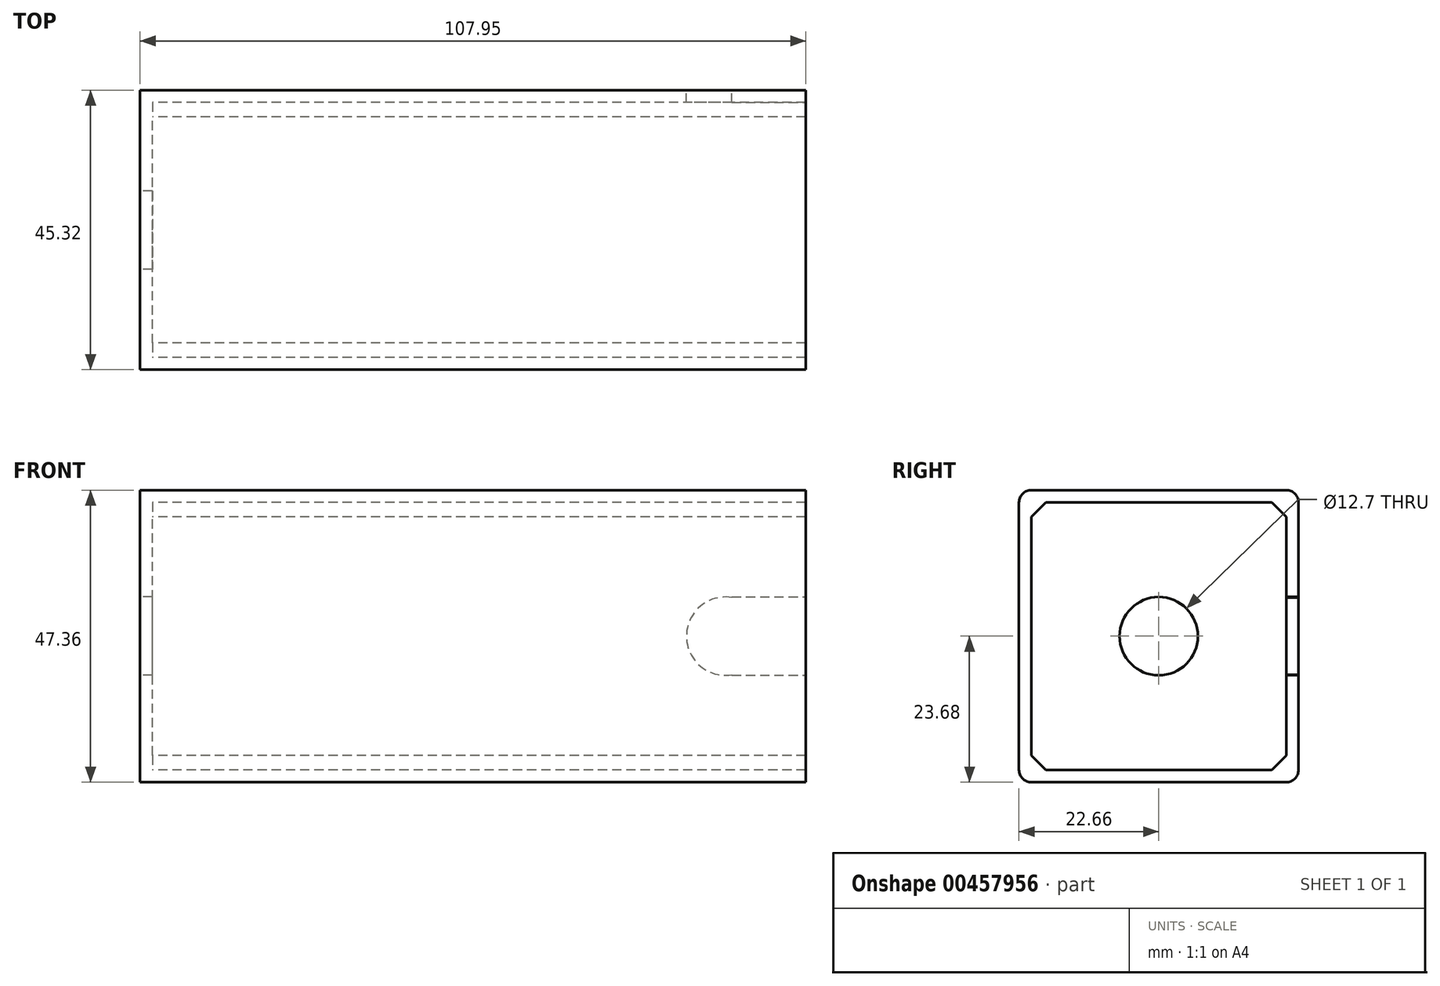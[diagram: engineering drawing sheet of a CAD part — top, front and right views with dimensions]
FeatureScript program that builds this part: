
annotation { "Feature Type Name" : "Feature", "Feature Type Description" : "" }
export const myFeature = defineFeature(function(context is Context, id is Id, definition is map)
    precondition{}
    {
        {
            assignVariable(context, id + "F0", {"name" : "WallWidth", "anyValue" : 2 * mm});
        }
        {
            var Q0;
            Q0=qCreatedBy(makeId("Right.planeOp"),FACE);
            var sketch = newSketch(context, id + "F1", { "sketchPlane" : qUnion([Q0])});
            skLineSegment(sketch, "E0.bottom", {"start": v(20.66, 21.68) * mm, "end": v(-20.66, 21.68) * mm});
            skLineSegment(sketch, "E0.top", {"start": v(20.66, -21.68) * mm, "end": v(-20.66, -21.68) * mm});
            skLineSegment(sketch, "E0.left", {"start": v(20.66, 21.68) * mm, "end": v(20.66, -21.68) * mm});
            skLineSegment(sketch, "E0.right", {"start": v(-20.66, 21.68) * mm, "end": v(-20.66, -21.68) * mm});
            skPoint(sketch, "E0.middle", {"position": v(0, 0) * mm});
            skLineSegment(sketch, "E1", {"start": v(-20.66, -19.34) * mm, "end": v(-18.32, -21.68) * mm});
            skLineSegment(sketch, "E2", {"start": v(18.32, -21.68) * mm, "end": v(20.65, -19.34) * mm});
            skLineSegment(sketch, "E3", {"start": v(-20.65, 19.34) * mm, "end": v(-18.32, 21.68) * mm});
            skLineSegment(sketch, "E4", {"start": v(18.32, 21.68) * mm, "end": v(20.65, 19.34) * mm});
            skLineSegment(sketch, "E5.bottom", {"start": v(-22.66, 23.68) * mm, "end": v(22.66, 23.68) * mm});
            skLineSegment(sketch, "E5.top", {"start": v(-22.66, -23.68) * mm, "end": v(22.66, -23.68) * mm});
            skLineSegment(sketch, "E5.left", {"start": v(-22.66, 23.68) * mm, "end": v(-22.66, -23.68) * mm});
            skLineSegment(sketch, "E5.right", {"start": v(22.66, 23.68) * mm, "end": v(22.66, -23.68) * mm});
            skSolve(sketch);
        }
        {
            var Q0;
            Q0=makeQuery(id+"F1.imprint","IMPRINT",FACE,{"disambiguationData":[TD([[makeQuery(id+"F1.imprint","IMPRINT",EDGE,{"derivedFrom":sQuery(id+"F1.wireOp",EDGE,"E5.bottom")}),-1.0]])]});
            var Q1;
            {var subQ0=sQuery(id+"F1.wireOp",EDGE,"E1");Q1=makeQuery(id+"F1.imprint","IMPRINT",FACE,{"disambiguationData":[TD([[makeQuery(id+"F1.imprint","IMPRINT",EDGE,{"derivedFrom":subQ0}),1.0]])]});}
            var Q2;
            {var subQ3=sQuery(id+"F1.wireOp",EDGE,"E1");Q2=makeQuery(id+"F1.imprint","IMPRINT",FACE,{"disambiguationData":[TD([[makeQuery(id+"F1.imprint","IMPRINT",EDGE,{"derivedFrom":subQ3}),-1.0]])]});}
            var Q3;
            {var subQ3=sQuery(id+"F1.wireOp",EDGE,"E2");Q3=makeQuery(id+"F1.imprint","IMPRINT",FACE,{"disambiguationData":[TD([[makeQuery(id+"F1.imprint","IMPRINT",EDGE,{"derivedFrom":subQ3}),-1.0]])]});}
            var Q4;
            {var subQ3=sQuery(id+"F1.wireOp",EDGE,"E4");Q4=makeQuery(id+"F1.imprint","IMPRINT",FACE,{"disambiguationData":[TD([[makeQuery(id+"F1.imprint","IMPRINT",EDGE,{"derivedFrom":subQ3}),1.0]])]});}
            var Q5;
            {var subQ3=sQuery(id+"F1.wireOp",EDGE,"E3");Q5=makeQuery(id+"F1.imprint","IMPRINT",FACE,{"disambiguationData":[TD([[makeQuery(id+"F1.imprint","IMPRINT",EDGE,{"derivedFrom":subQ3}),1.0]])]});}
            extrude(context, id + "F2", {"entities" : qUnion([Q0, Q1, Q2, Q3, Q4, Q5]), "depth" : getVariable(context, 'WallWidth')});
        }
        {
            var Q0;
            Q0=makeQuery(id+"F1.imprint","IMPRINT",FACE,{"disambiguationData":[TD([[makeQuery(id+"F1.imprint","IMPRINT",EDGE,{"derivedFrom":sQuery(id+"F1.wireOp",EDGE,"E5.bottom")}),-1.0]])]});
            var Q1;
            {var subQ3=sQuery(id+"F1.wireOp",EDGE,"E4");Q1=makeQuery(id+"F1.imprint","IMPRINT",FACE,{"disambiguationData":[TD([[makeQuery(id+"F1.imprint","IMPRINT",EDGE,{"derivedFrom":subQ3}),1.0]])]});}
            var Q2;
            {var subQ3=sQuery(id+"F1.wireOp",EDGE,"E2");Q2=makeQuery(id+"F1.imprint","IMPRINT",FACE,{"disambiguationData":[TD([[makeQuery(id+"F1.imprint","IMPRINT",EDGE,{"derivedFrom":subQ3}),-1.0]])]});}
            var Q3;
            {var subQ3=sQuery(id+"F1.wireOp",EDGE,"E1");Q3=makeQuery(id+"F1.imprint","IMPRINT",FACE,{"disambiguationData":[TD([[makeQuery(id+"F1.imprint","IMPRINT",EDGE,{"derivedFrom":subQ3}),-1.0]])]});}
            var Q4;
            {var subQ3=sQuery(id+"F1.wireOp",EDGE,"E3");Q4=makeQuery(id+"F1.imprint","IMPRINT",FACE,{"disambiguationData":[TD([[makeQuery(id+"F1.imprint","IMPRINT",EDGE,{"derivedFrom":subQ3}),1.0]])]});}
            extrude(context, id + "F3", {"entities" : qUnion([Q0, Q1, Q2, Q3, Q4]), "operationType" : NewBodyOperationType.ADD, "depth" : 107.95 * mm});
        }
        {
            var Q0;
            Q0 = qSketchRegion(id + "F1", true);
            var sketch = newSketch(context, id + "F4", { "sketchPlane" : qUnion([Q0])});
            skCircle(sketch, "E6", {"center": v(0, 0) * mm, "radius": 6.35 * mm});
            skSolve(sketch);
        }
        {
            var Q0;
            Q0 = qSketchRegion(id + "F4", true);
            var sketch = newSketch(context, id + "F5", { "sketchPlane" : qUnion([Q0])});
            skSolve(sketch);
        }
        {
            var Q0;
            {var subQ0=sQuery(id+"F1.wireOp",EDGE,"E1");Q0=makeQuery(id+"F1.imprint","IMPRINT",FACE,{"disambiguationData":[TD([[makeQuery(id+"F1.imprint","IMPRINT",EDGE,{"derivedFrom":subQ0}),1.0]])]});}
            var sketch = newSketch(context, id + "F6", { "sketchPlane" : qUnion([Q0])});
            skSolve(sketch);
        }
        {
            var Q0;
            Q0 = qSketchRegion(id + "F5", true);
            var Q1;
            Q1=makeQuery(id+"F4.imprint","IMPRINT",FACE,{"disambiguationData":[TD([[makeQuery(id+"F4.imprint","IMPRINT",EDGE,{"derivedFrom":sQuery(id+"F4.wireOp",EDGE,"E6")}),1.0]])]});
            extrude(context, id + "F7", {"entities" : qUnion([Q0, Q1]), "operationType" : NewBodyOperationType.REMOVE, "endBound" : BoundingType.THROUGH_ALL, "depth" : 25 * mm});
        }
        {
            var Q0;
            {var subQ0=sQuery(id+"F1.wireOp",EDGE,"E5.right");Q0=makeQuery(id+"F3.boolean.opBoolean","MERGE",FACE,{"derivedFrom":[makeQuery(id+"F2.opExtrude","SWEPT_FACE",FACE,{"disambiguationData":[OSD([subQ0])]}),makeQuery(id+"F3.opExtrude","SWEPT_FACE",FACE,{"disambiguationData":[OSD([subQ0])]})]});}
            var sketch = newSketch(context, id + "F8", { "sketchPlane" : qUnion([Q0])});
            skCircle(sketch, "E7", {"center": v(-94.95, 0) * mm, "radius": 6.35 * mm});
            skSolve(sketch);
        }
        {
            var Q0;
            Q0=makeQuery(id+"F8.imprint","IMPRINT",FACE,{"disambiguationData":[TD([[makeQuery(id+"F8.imprint","IMPRINT",EDGE,{"derivedFrom":sQuery(id+"F8.wireOp",EDGE,"E7")}),1.0]])]});
            extrude(context, id + "F9", {"entities" : qUnion([Q0]), "operationType" : NewBodyOperationType.REMOVE, "oppositeDirection" : true, "depth" : 25 * mm});
        }
        {
            var Q0;
            {var subQ0=sQuery(id+"F1.wireOp",EDGE,"E5.left");var subQ1=sQuery(id+"F1.wireOp",EDGE,"E5.bottom");Q0=makeQuery(id+"F3.boolean.opBoolean","MERGE",EDGE,{"derivedFrom":[makeQuery(id+"F2.opExtrude","SWEPT_EDGE",EDGE,{"disambiguationData":[OSD([subQ1,subQ0])]}),makeQuery(id+"F3.opExtrude","SWEPT_EDGE",EDGE,{"disambiguationData":[OSD([subQ1,subQ0])]})]});}
            var Q1;
            {var subQ0=sQuery(id+"F1.wireOp",EDGE,"E5.right");var subQ1=sQuery(id+"F1.wireOp",EDGE,"E5.bottom");Q1=makeQuery(id+"F3.boolean.opBoolean","MERGE",EDGE,{"derivedFrom":[makeQuery(id+"F2.opExtrude","SWEPT_EDGE",EDGE,{"disambiguationData":[OSD([subQ1,subQ0])]}),makeQuery(id+"F3.opExtrude","SWEPT_EDGE",EDGE,{"disambiguationData":[OSD([subQ1,subQ0])]})]});}
            var Q2;
            {var subQ0=sQuery(id+"F1.wireOp",EDGE,"E5.right");var subQ1=sQuery(id+"F1.wireOp",EDGE,"E5.top");Q2=makeQuery(id+"F3.boolean.opBoolean","MERGE",EDGE,{"derivedFrom":[makeQuery(id+"F2.opExtrude","SWEPT_EDGE",EDGE,{"disambiguationData":[OSD([subQ1,subQ0])]}),makeQuery(id+"F3.opExtrude","SWEPT_EDGE",EDGE,{"disambiguationData":[OSD([subQ1,subQ0])]})]});}
            var Q3;
            {var subQ0=sQuery(id+"F1.wireOp",EDGE,"E5.left");var subQ1=sQuery(id+"F1.wireOp",EDGE,"E5.top");Q3=makeQuery(id+"F3.boolean.opBoolean","MERGE",EDGE,{"derivedFrom":[makeQuery(id+"F2.opExtrude","SWEPT_EDGE",EDGE,{"disambiguationData":[OSD([subQ1,subQ0])]}),makeQuery(id+"F3.opExtrude","SWEPT_EDGE",EDGE,{"disambiguationData":[OSD([subQ1,subQ0])]})]});}
            fillet(context, id + "F10", {"entities" : qUnion([Q0, Q1, Q2, Q3]), "radius" : 2 * mm, "tangentPropagation" : true, "allowEdgeOverflow" : false});
        }
        {
            var Q0;
            Q0=makeQuery(id+"F3.opExtrude","CAP_FACE",FACE,{"disambiguationData":[OSD([sQuery(id+"F1.wireOp",EDGE,"E0.bottom"),sQuery(id+"F1.wireOp",EDGE,"E0.top"),sQuery(id+"F1.wireOp",EDGE,"E0.left"),sQuery(id+"F1.wireOp",EDGE,"E0.right"),sQuery(id+"F1.wireOp",EDGE,"E1"),sQuery(id+"F1.wireOp",EDGE,"E2"),sQuery(id+"F1.wireOp",EDGE,"E3"),sQuery(id+"F1.wireOp",EDGE,"E4"),sQuery(id+"F1.wireOp",EDGE,"E5.bottom"),sQuery(id+"F1.wireOp",EDGE,"E5.top"),sQuery(id+"F1.wireOp",EDGE,"E5.left"),sQuery(id+"F1.wireOp",EDGE,"E5.right")])],"isStart":false});
            var sketch = newSketch(context, id + "F11", { "sketchPlane" : qUnion([Q0])});
            skLineSegment(sketch, "E8.bottom", {"start": v(22.66, -6.35) * mm, "end": v(20.66, -6.35) * mm});
            skLineSegment(sketch, "E8.top", {"start": v(22.66, 6.35) * mm, "end": v(20.66, 6.35) * mm});
            skLineSegment(sketch, "E8.left", {"start": v(22.66, -6.35) * mm, "end": v(22.66, 6.35) * mm});
            skLineSegment(sketch, "E8.right", {"start": v(20.66, -6.35) * mm, "end": v(20.66, 6.35) * mm});
            skPoint(sketch, "E9", {"position": v(20.66, 0) * mm});
            skSolve(sketch);
        }
        {
            var Q0;
            Q0=makeQuery(id+"F11.imprint","IMPRINT",FACE,{"disambiguationData":[TD([[makeQuery(id+"F11.imprint","IMPRINT",EDGE,{"derivedFrom":sQuery(id+"F11.wireOp",EDGE,"E8.bottom")}),-1.0]])]});
            extrude(context, id + "F12", {"entities" : qUnion([Q0]), "operationType" : NewBodyOperationType.REMOVE, "oppositeDirection" : true, "depth" : 12 * mm});
        }
    });
